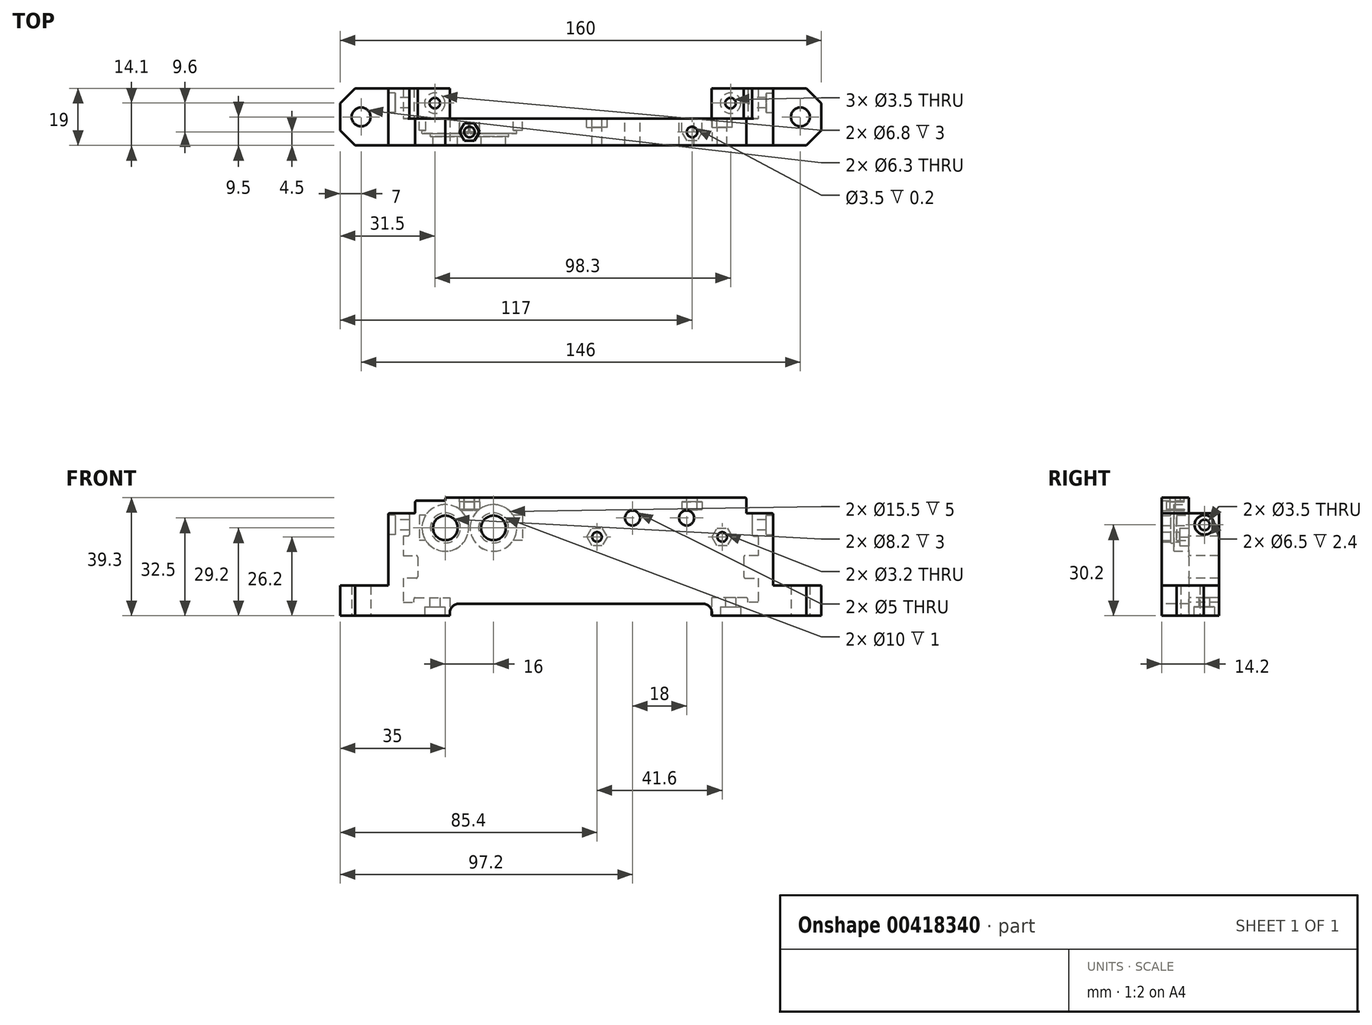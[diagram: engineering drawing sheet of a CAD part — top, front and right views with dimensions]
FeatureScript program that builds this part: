
annotation { "Feature Type Name" : "Feature", "Feature Type Description" : "" }
export const myFeature = defineFeature(function(context is Context, id is Id, definition is map)
    precondition{}
    {
        {
            var Q0;
            Q0=qCreatedBy(makeId("Front.planeOp"),FACE);
            var sketch = newSketch(context, id + "F0", { "sketchPlane" : qUnion([Q0])});
            skLineSegment(sketch, "E0", {"start": v(-64, 28) * mm, "end": v(-57.5, 28) * mm});
            skLineSegment(sketch, "E1", {"start": v(-57, 27.5) * mm, "end": v(-57, 21) * mm});
            skLineSegment(sketch, "E2", {"start": v(-57.5, 20.5) * mm, "end": v(-59, 20.5) * mm});
            skLineSegment(sketch, "E3", {"start": v(-59, 20.5) * mm, "end": v(-59, 14) * mm});
            skLineSegment(sketch, "E4", {"start": v(-59, 14) * mm, "end": v(-54.7, 14) * mm});
            skLineSegment(sketch, "E5", {"start": v(-54.2, 13.5) * mm, "end": v(-54.2, 7) * mm});
            skLineSegment(sketch, "E6", {"start": v(-54.7, 6.5) * mm, "end": v(-59, 6.5) * mm});
            skLineSegment(sketch, "E7", {"start": v(-59, 6.5) * mm, "end": v(-59, -1.5) * mm});
            skLineSegment(sketch, "E8", {"start": v(-59, -1.5) * mm, "end": v(-55.5, -1.5) * mm});
            skLineSegment(sketch, "E9", {"start": v(-55.5, -1.5) * mm, "end": v(-55.5, -0.5) * mm});
            skLineSegment(sketch, "E10", {"start": v(-55, 0) * mm, "end": v(-43.5, 0) * mm});
            skLineSegment(sketch, "E11", {"start": v(-43.5, 0) * mm, "end": v(-43.5, -6) * mm});
            skLineSegment(sketch, "E12", {"start": v(-43.5, -6) * mm, "end": v(-64, -6) * mm});
            skLineSegment(sketch, "E13", {"start": v(-64, -6) * mm, "end": v(-64, 28) * mm});
            skLineSegment(sketch, "E14", {"start": v(0, 0) * mm, "end": v(0, 39.92) * mm, "construction": true});
            skPoint(sketch, "E15.visualSharp", {"position": v(-54.2, 14) * mm});
            skArc(sketch, "E15.filletArc", {"start": v(-54.2, 13.5) * mm, "mid": v(-54.35, 13.85) * mm, "end": v(-54.7, 14) * mm});
            skPoint(sketch, "E16.visualSharp", {"position": v(-54.2, 6.5) * mm});
            skArc(sketch, "E16.filletArc", {"start": v(-54.7, 6.5) * mm, "mid": v(-54.35, 6.65) * mm, "end": v(-54.2, 7) * mm});
            skPoint(sketch, "E17.visualSharp", {"position": v(-55.5, 0) * mm});
            skArc(sketch, "E17.filletArc", {"start": v(-55, 0) * mm, "mid": v(-55.35, -0.15) * mm, "end": v(-55.5, -0.5) * mm});
            skPoint(sketch, "E18.visualSharp", {"position": v(-57, 28) * mm});
            skArc(sketch, "E18.filletArc", {"start": v(-57, 27.5) * mm, "mid": v(-57.15, 27.85) * mm, "end": v(-57.5, 28) * mm});
            skPoint(sketch, "E19.visualSharp", {"position": v(-57, 20.5) * mm});
            skArc(sketch, "E19.filletArc", {"start": v(-57.5, 20.5) * mm, "mid": v(-57.15, 20.65) * mm, "end": v(-57, 21) * mm});
            skLineSegment(sketch, "E20.MirrorCS", {"start": v(64, -6) * mm, "end": v(64, 28) * mm});
            skLineSegment(sketch, "E21.MirrorCS", {"start": v(43.5, -6) * mm, "end": v(64, -6) * mm});
            skLineSegment(sketch, "E22.MirrorCS", {"start": v(43.5, 0) * mm, "end": v(43.5, -6) * mm});
            skLineSegment(sketch, "E23.MirrorCS", {"start": v(55, 0) * mm, "end": v(43.5, 0) * mm});
            skArc(sketch, "E24.MirrorCS", {"start": v(55, 0) * mm, "mid": v(55.35, -0.15) * mm, "end": v(55.5, -0.5) * mm});
            skLineSegment(sketch, "E25.MirrorCS", {"start": v(55.5, -1.5) * mm, "end": v(55.5, -0.5) * mm});
            skLineSegment(sketch, "E26.MirrorCS", {"start": v(59, -1.5) * mm, "end": v(55.5, -1.5) * mm});
            skLineSegment(sketch, "E27.MirrorCS", {"start": v(59, 6.5) * mm, "end": v(59, -1.5) * mm});
            skLineSegment(sketch, "E28.MirrorCS", {"start": v(54.7, 6.5) * mm, "end": v(59, 6.5) * mm});
            skArc(sketch, "E29.MirrorCS", {"start": v(54.7, 6.5) * mm, "mid": v(54.35, 6.65) * mm, "end": v(54.2, 7) * mm});
            skLineSegment(sketch, "E30.MirrorCS", {"start": v(54.2, 13.5) * mm, "end": v(54.2, 7) * mm});
            skArc(sketch, "E31.MirrorCS", {"start": v(54.2, 13.5) * mm, "mid": v(54.35, 13.85) * mm, "end": v(54.7, 14) * mm});
            skLineSegment(sketch, "E32.MirrorCS", {"start": v(59, 14) * mm, "end": v(54.7, 14) * mm});
            skLineSegment(sketch, "E33.MirrorCS", {"start": v(59, 20.5) * mm, "end": v(59, 14) * mm});
            skLineSegment(sketch, "E34.MirrorCS", {"start": v(57.5, 20.5) * mm, "end": v(59, 20.5) * mm});
            skArc(sketch, "E35.MirrorCS", {"start": v(57.5, 20.5) * mm, "mid": v(57.15, 20.65) * mm, "end": v(57, 21) * mm});
            skLineSegment(sketch, "E36.MirrorCS", {"start": v(57, 27.5) * mm, "end": v(57, 21) * mm});
            skArc(sketch, "E37.MirrorCS", {"start": v(57, 27.5) * mm, "mid": v(57.15, 27.85) * mm, "end": v(57.5, 28) * mm});
            skLineSegment(sketch, "E38.MirrorCS", {"start": v(64, 28) * mm, "end": v(57.5, 28) * mm});
            skSolve(sketch);
        }
        {
            var Q0;
            Q0=makeQuery(id+"F0.imprint","IMPRINT",FACE,{"disambiguationData":[TD([[makeQuery(id+"F0.imprint","IMPRINT",EDGE,{"derivedFrom":sQuery(id+"F0.wireOp",EDGE,"E0")}),-1.0]])]});
            var sketch = newSketch(context, id + "F1", { "sketchPlane" : qUnion([Q0])});
            skLineSegment(sketch, "E39", {"start": v(-64, 28) * mm, "end": v(-64, -6) * mm});
            skLineSegment(sketch, "E40", {"start": v(-64, -6) * mm, "end": v(0, -6) * mm});
            skLineSegment(sketch, "E41", {"start": v(-64, 28) * mm, "end": v(-55, 28) * mm});
            skLineSegment(sketch, "E42", {"start": v(-55, 28) * mm, "end": v(-55, 32.2) * mm});
            skLineSegment(sketch, "E43", {"start": v(-55, 32.2) * mm, "end": v(0, 32.2) * mm});
            skLineSegment(sketch, "E44.MirrorCS", {"start": v(55, 32.2) * mm, "end": v(0, 32.2) * mm});
            skLineSegment(sketch, "E45.MirrorCS", {"start": v(64, -6) * mm, "end": v(0, -6) * mm});
            skLineSegment(sketch, "E46.MirrorCS", {"start": v(64, 28) * mm, "end": v(64, -6) * mm});
            skLineSegment(sketch, "E47.MirrorCS", {"start": v(64, 28) * mm, "end": v(55, 28) * mm});
            skLineSegment(sketch, "E48.MirrorCS", {"start": v(55, 28) * mm, "end": v(55, 32.2) * mm});
            skSolve(sketch);
        }
        {
            var Q0;
            Q0 = qSketchRegion(id + "F1", true);
            extrude(context, id + "F2", {"entities" : qUnion([Q0]), "depth" : 9 * mm});
        }
        {
            var Q0;
            Q0 = qSketchRegion(id + "F0", true);
            extrude(context, id + "F3", {"entities" : qUnion([Q0]), "operationType" : NewBodyOperationType.ADD, "oppositeDirection" : true, "depth" : 10 * mm});
        }
        {
            var Q0;
            Q0=qCreatedBy(makeId("Front.planeOp"),FACE);
            var sketch = newSketch(context, id + "F4", { "sketchPlane" : qUnion([Q0])});
            skCircle(sketch, "E49", {"center": v(-29, 23.2) * mm, "radius": 4.1 * mm});
            skCircle(sketch, "E50", {"center": v(-45, 23.2) * mm, "radius": 4.1 * mm});
            skCircle(sketch, "E51", {"center": v(47, 20.2) * mm, "radius": 1.6 * mm});
            skCircle(sketch, "E52", {"center": v(5.4, 20.2) * mm, "radius": 1.6 * mm});
            skCircle(sketch, "E53.cCircle", {"center": v(5.4, 20.2) * mm, "radius": 2.93 * mm, "construction": true});
            skLineSegment(sketch, "E53.0", {"start": v(7.09, 17.28) * mm, "end": v(3.71, 17.28) * mm});
            skLineSegment(sketch, "E53.1", {"start": v(3.71, 17.28) * mm, "end": v(2.02, 20.2) * mm});
            skLineSegment(sketch, "E53.2", {"start": v(2.02, 20.2) * mm, "end": v(3.71, 23.13) * mm});
            skLineSegment(sketch, "E53.3", {"start": v(3.71, 23.13) * mm, "end": v(7.09, 23.13) * mm});
            skLineSegment(sketch, "E53.4", {"start": v(7.09, 23.13) * mm, "end": v(8.78, 20.2) * mm});
            skLineSegment(sketch, "E53.5", {"start": v(8.78, 20.2) * mm, "end": v(7.09, 17.28) * mm});
            skPoint(sketch, "E53.0.midPoint", {"position": v(5.4, 17.28) * mm});
            skCircle(sketch, "E54.cCircle", {"center": v(47, 20.2) * mm, "radius": 2.93 * mm, "construction": true});
            skLineSegment(sketch, "E54.0", {"start": v(48.69, 17.28) * mm, "end": v(45.31, 17.28) * mm});
            skLineSegment(sketch, "E54.1", {"start": v(45.31, 17.28) * mm, "end": v(43.62, 20.2) * mm});
            skLineSegment(sketch, "E54.2", {"start": v(43.62, 20.2) * mm, "end": v(45.31, 23.13) * mm});
            skLineSegment(sketch, "E54.3", {"start": v(45.31, 23.13) * mm, "end": v(48.69, 23.13) * mm});
            skLineSegment(sketch, "E54.4", {"start": v(48.69, 23.13) * mm, "end": v(50.38, 20.2) * mm});
            skLineSegment(sketch, "E54.5", {"start": v(50.38, 20.2) * mm, "end": v(48.69, 17.28) * mm});
            skPoint(sketch, "E54.0.midPoint", {"position": v(47, 17.28) * mm});
            skCircle(sketch, "E55", {"center": v(-45, 23.2) * mm, "radius": 5 * mm});
            skCircle(sketch, "E56", {"center": v(-29, 23.2) * mm, "radius": 5 * mm});
            skCircle(sketch, "E57", {"center": v(35.2, 26.5) * mm, "radius": 2.5 * mm});
            skCircle(sketch, "E58", {"center": v(17.2, 26.5) * mm, "radius": 2.5 * mm});
            skCircle(sketch, "E59", {"center": v(-45, 23.2) * mm, "radius": 7.75 * mm});
            skCircle(sketch, "E60", {"center": v(-29, 23.2) * mm, "radius": 7.75 * mm});
            skSolve(sketch);
        }
        {
            var Q0;
            Q0=makeQuery(id+"F4.imprint","IMPRINT",FACE,{"disambiguationData":[TD([[makeQuery(id+"F4.imprint","IMPRINT",EDGE,{"derivedFrom":sQuery(id+"F4.wireOp",EDGE,"E49")}),1.0]])]});
            var Q1;
            Q1=makeQuery(id+"F4.imprint","IMPRINT",FACE,{"disambiguationData":[TD([[makeQuery(id+"F4.imprint","IMPRINT",EDGE,{"derivedFrom":sQuery(id+"F4.wireOp",EDGE,"E50")}),1.0]])]});
            var Q2;
            Q2=makeQuery(id+"F4.imprint","IMPRINT",FACE,{"disambiguationData":[TD([[makeQuery(id+"F4.imprint","IMPRINT",EDGE,{"derivedFrom":sQuery(id+"F4.wireOp",EDGE,"E57")}),1.0]])]});
            var Q3;
            Q3=makeQuery(id+"F4.imprint","IMPRINT",FACE,{"disambiguationData":[TD([[makeQuery(id+"F4.imprint","IMPRINT",EDGE,{"derivedFrom":sQuery(id+"F4.wireOp",EDGE,"E58")}),1.0]])]});
            var Q4;
            Q4=makeQuery(id+"F4.imprint","IMPRINT",FACE,{"disambiguationData":[TD([[makeQuery(id+"F4.imprint","IMPRINT",EDGE,{"derivedFrom":sQuery(id+"F4.wireOp",EDGE,"E52")}),1.0]])]});
            var Q5;
            Q5=makeQuery(id+"F4.imprint","IMPRINT",FACE,{"disambiguationData":[TD([[makeQuery(id+"F4.imprint","IMPRINT",EDGE,{"derivedFrom":sQuery(id+"F4.wireOp",EDGE,"E51")}),1.0]])]});
            extrude(context, id + "F5", {"entities" : qUnion([Q0, Q1, Q2, Q3, Q4, Q5]), "operationType" : NewBodyOperationType.REMOVE, "depth" : 24.8 * mm});
        }
        {
            var Q0;
            Q0=makeQuery(id+"F4.imprint","IMPRINT",FACE,{"disambiguationData":[TD([[makeQuery(id+"F4.imprint","IMPRINT",EDGE,{"derivedFrom":sQuery(id+"F4.wireOp",EDGE,"E52")}),-1.0]])]});
            var Q1;
            Q1=makeQuery(id+"F4.imprint","IMPRINT",FACE,{"disambiguationData":[TD([[makeQuery(id+"F4.imprint","IMPRINT",EDGE,{"derivedFrom":sQuery(id+"F4.wireOp",EDGE,"E51")}),-1.0]])]});
            extrude(context, id + "F6", {"entities" : qUnion([Q0, Q1]), "operationType" : NewBodyOperationType.REMOVE, "depth" : 3 * mm});
        }
        {
            var Q0;
            Q0=makeQuery(id+"F4.imprint","IMPRINT",FACE,{"disambiguationData":[TD([[makeQuery(id+"F4.imprint","IMPRINT",EDGE,{"derivedFrom":sQuery(id+"F4.wireOp",EDGE,"E50")}),-1.0]])]});
            var Q1;
            Q1=makeQuery(id+"F4.imprint","IMPRINT",FACE,{"disambiguationData":[TD([[makeQuery(id+"F4.imprint","IMPRINT",EDGE,{"derivedFrom":sQuery(id+"F4.wireOp",EDGE,"E49")}),-1.0]])]});
            extrude(context, id + "F7", {"entities" : qUnion([Q0, Q1]), "operationType" : NewBodyOperationType.REMOVE, "depth" : 6 * mm});
        }
        {
            var Q0;
            Q0=makeQuery(id+"F4.imprint","IMPRINT",FACE,{"disambiguationData":[TD([[makeQuery(id+"F4.imprint","IMPRINT",EDGE,{"derivedFrom":sQuery(id+"F4.wireOp",EDGE,"E56")}),-1.0]])]});
            var Q1;
            Q1=makeQuery(id+"F4.imprint","IMPRINT",FACE,{"disambiguationData":[TD([[makeQuery(id+"F4.imprint","IMPRINT",EDGE,{"derivedFrom":sQuery(id+"F4.wireOp",EDGE,"E55")}),-1.0]])]});
            extrude(context, id + "F8", {"entities" : qUnion([Q0, Q1]), "operationType" : NewBodyOperationType.REMOVE, "depth" : 5 * mm});
        }
        {
            var Q0;
            Q0=makeQuery(id+"F3.boolean.opBoolean","MERGE",FACE,{"derivedFrom":[makeQuery(id+"F2.opExtrude","SWEPT_FACE",FACE,{"disambiguationData":[OSD([sQuery(id+"F1.wireOp",EDGE,"E39")])]}),makeQuery(id+"F3.opExtrude","SWEPT_FACE",FACE,{"disambiguationData":[OSD([sQuery(id+"F0.wireOp",EDGE,"E13")])]})]});
            var sketch = newSketch(context, id + "F9", { "sketchPlane" : qUnion([Q0])});
            skCircle(sketch, "E61", {"center": v(-5.2, 24.2) * mm, "radius": 1.75 * mm});
            skCircle(sketch, "E62", {"center": v(-5.2, 24.2) * mm, "radius": 3.25 * mm});
            skSolve(sketch);
        }
        {
            var Q0;
            Q0=makeQuery(id+"F9.imprint","IMPRINT",FACE,{"disambiguationData":[TD([[makeQuery(id+"F9.imprint","IMPRINT",EDGE,{"derivedFrom":sQuery(id+"F9.wireOp",EDGE,"E61")}),1.0]])]});
            extrude(context, id + "F10", {"entities" : qUnion([Q0]), "operationType" : NewBodyOperationType.REMOVE, "oppositeDirection" : true, "depth" : 158.2 * mm});
        }
        {
            var Q0;
            Q0=makeQuery(id+"F9.imprint","IMPRINT",FACE,{"disambiguationData":[TD([[makeQuery(id+"F9.imprint","IMPRINT",EDGE,{"derivedFrom":sQuery(id+"F9.wireOp",EDGE,"E61")}),-1.0]])]});
            extrude(context, id + "F11", {"entities" : qUnion([Q0]), "operationType" : NewBodyOperationType.REMOVE, "oppositeDirection" : true, "depth" : 2.4 * mm});
        }
        {
            var Q0;
            Q0=makeQuery(id+"F3.boolean.opBoolean","MERGE",FACE,{"derivedFrom":[makeQuery(id+"F2.opExtrude","SWEPT_FACE",FACE,{"disambiguationData":[OSD([sQuery(id+"F1.wireOp",EDGE,"E46.MirrorCS")])]}),makeQuery(id+"F3.opExtrude","SWEPT_FACE",FACE,{"disambiguationData":[OSD([sQuery(id+"F0.wireOp",EDGE,"E20.MirrorCS")])]})]});
            var sketch = newSketch(context, id + "F12", { "sketchPlane" : qUnion([Q0])});
            skCircle(sketch, "E63", {"center": v(5.2, 24.2) * mm, "radius": 3.25 * mm});
            skSolve(sketch);
        }
        {
            var Q0;
            Q0 = qSketchRegion(id + "F12", true);
            extrude(context, id + "F13", {"entities" : qUnion([Q0]), "operationType" : NewBodyOperationType.REMOVE, "oppositeDirection" : true, "depth" : 2.4 * mm});
        }
        {
            var Q0;
            Q0=makeQuery(id+"F3.boolean.opBoolean","MERGE",FACE,{"derivedFrom":[makeQuery(id+"F2.opExtrude","SWEPT_FACE",FACE,{"disambiguationData":[OSD([sQuery(id+"F1.wireOp",EDGE,"E40"),sQuery(id+"F1.wireOp",EDGE,"E45.MirrorCS")])]}),makeQuery(id+"F3.opExtrude","SWEPT_FACE",FACE,{"disambiguationData":[OSD([sQuery(id+"F0.wireOp",EDGE,"E12")])]}),makeQuery(id+"F3.opExtrude","SWEPT_FACE",FACE,{"disambiguationData":[OSD([sQuery(id+"F0.wireOp",EDGE,"E21.MirrorCS")])]})]});
            var sketch = newSketch(context, id + "F14", { "sketchPlane" : qUnion([Q0])});
            skCircle(sketch, "E64", {"center": v(49.8, -5.1) * mm, "radius": 1.75 * mm});
            skCircle(sketch, "E65", {"center": v(49.8, -5.1) * mm, "radius": 3.4 * mm});
            skCircle(sketch, "E66", {"center": v(-48.5, -5.1) * mm, "radius": 1.75 * mm});
            skCircle(sketch, "E67", {"center": v(-48.5, -5.1) * mm, "radius": 3.4 * mm});
            skSolve(sketch);
        }
        {
            var Q0;
            Q0 = qSketchRegion(id + "F14", true);
            var Q1;
            Q1=makeQuery(id+"F14.imprint","IMPRINT",FACE,{"disambiguationData":[TD([[makeQuery(id+"F14.imprint","IMPRINT",EDGE,{"derivedFrom":sQuery(id+"F14.wireOp",EDGE,"E64")}),1.0]])]});
            extrude(context, id + "F15", {"entities" : qUnion([Q0, Q1]), "operationType" : NewBodyOperationType.REMOVE, "oppositeDirection" : true, "depth" : 3 * mm});
        }
        {
            var Q0;
            Q0=makeQuery(id+"F14.imprint","IMPRINT",FACE,{"disambiguationData":[TD([[makeQuery(id+"F14.imprint","IMPRINT",EDGE,{"derivedFrom":sQuery(id+"F14.wireOp",EDGE,"E64")}),1.0]])]});
            var Q1;
            Q1=makeQuery(id+"F14.imprint","IMPRINT",FACE,{"disambiguationData":[TD([[makeQuery(id+"F14.imprint","IMPRINT",EDGE,{"derivedFrom":sQuery(id+"F14.wireOp",EDGE,"E66")}),1.0]])]});
            extrude(context, id + "F16", {"entities" : qUnion([Q0, Q1]), "operationType" : NewBodyOperationType.REMOVE, "oppositeDirection" : true, "depth" : 25 * mm});
        }
        {
            var Q0;
            Q0=makeQuery(id+"F2.opExtrude","SWEPT_FACE",FACE,{"disambiguationData":[OSD([sQuery(id+"F1.wireOp",EDGE,"E43"),sQuery(id+"F1.wireOp",EDGE,"E44.MirrorCS")])]});
            var sketch = newSketch(context, id + "F17", { "sketchPlane" : qUnion([Q0])});
            skLineSegment(sketch, "E68.bottom", {"start": v(55, -9) * mm, "end": v(-45, -9) * mm});
            skLineSegment(sketch, "E68.top", {"start": v(55, 0) * mm, "end": v(-45, 0) * mm});
            skLineSegment(sketch, "E68.left", {"start": v(55, -9) * mm, "end": v(55, 0) * mm});
            skLineSegment(sketch, "E68.right", {"start": v(-45, -9) * mm, "end": v(-45, 0) * mm});
            skSolve(sketch);
        }
        {
            var Q0;
            Q0 = qSketchRegion(id + "F17", true);
            extrude(context, id + "F18", {"entities" : qUnion([Q0]), "operationType" : NewBodyOperationType.ADD, "depth" : 1.1 * mm});
        }
        {
            var Q0;
            Q0=makeQuery(id+"F18.opExtrude","CAP_FACE",FACE,{"disambiguationData":[OSD([sQuery(id+"F17.wireOp",EDGE,"E68.bottom"),sQuery(id+"F17.wireOp",EDGE,"E68.top"),sQuery(id+"F17.wireOp",EDGE,"E68.left"),sQuery(id+"F17.wireOp",EDGE,"E68.right")])],"isStart":false});
            var sketch = newSketch(context, id + "F19", { "sketchPlane" : qUnion([Q0])});
            skCircle(sketch, "E69", {"center": v(37, -4.5) * mm, "radius": 1.75 * mm});
            skCircle(sketch, "E70.cCircle", {"center": v(37, -4.5) * mm, "radius": 2.93 * mm, "construction": true});
            skLineSegment(sketch, "E70.0", {"start": v(38.69, -7.42) * mm, "end": v(35.31, -7.42) * mm});
            skLineSegment(sketch, "E70.1", {"start": v(35.31, -7.42) * mm, "end": v(33.62, -4.5) * mm});
            skLineSegment(sketch, "E70.2", {"start": v(33.62, -4.5) * mm, "end": v(35.31, -1.57) * mm});
            skLineSegment(sketch, "E70.3", {"start": v(35.31, -1.57) * mm, "end": v(38.69, -1.57) * mm});
            skLineSegment(sketch, "E70.4", {"start": v(38.69, -1.58) * mm, "end": v(40.38, -4.5) * mm});
            skLineSegment(sketch, "E70.5", {"start": v(40.38, -4.5) * mm, "end": v(38.69, -7.42) * mm});
            skPoint(sketch, "E70.0.midPoint", {"position": v(37, -7.42) * mm});
            skLineSegment(sketch, "E71", {"start": v(0, 6.74) * mm, "end": v(0, -15.63) * mm, "construction": true});
            skCircle(sketch, "E72.MirrorC", {"center": v(-37, -4.5) * mm, "radius": 1.75 * mm});
            skLineSegment(sketch, "E73.MirrorCS", {"start": v(-35.31, -7.43) * mm, "end": v(-33.62, -4.5) * mm});
            skLineSegment(sketch, "E74.MirrorCS", {"start": v(-33.62, -4.5) * mm, "end": v(-35.31, -1.58) * mm});
            skLineSegment(sketch, "E75.MirrorCS", {"start": v(-35.31, -1.58) * mm, "end": v(-38.69, -1.58) * mm});
            skLineSegment(sketch, "E76.MirrorCS", {"start": v(-38.69, -1.58) * mm, "end": v(-40.38, -4.5) * mm});
            skLineSegment(sketch, "E77.MirrorCS", {"start": v(-40.38, -4.5) * mm, "end": v(-38.69, -7.43) * mm});
            skLineSegment(sketch, "E78.MirrorCS", {"start": v(-38.69, -7.43) * mm, "end": v(-35.31, -7.43) * mm});
            skSolve(sketch);
        }
        {
            var Q0;
            Q0 = qSketchRegion(id + "F19", true);
            extrude(context, id + "F20", {"entities" : qUnion([Q0]), "operationType" : NewBodyOperationType.REMOVE, "oppositeDirection" : true, "depth" : 4 * mm, "hasSecondDirection" : true, "secondDirectionOppositeDirection" : true, "secondDirectionDepth" : (3.9 - 2.5) * mm});
        }
        {
            var Q0;
            Q0=makeQuery(id+"F19.imprint","IMPRINT",FACE,{"disambiguationData":[TD([[makeQuery(id+"F19.imprint","IMPRINT",EDGE,{"derivedFrom":sQuery(id+"F19.wireOp",EDGE,"E72.MirrorC")}),-1.0]])]});
            var Q1;
            Q1=makeQuery(id+"F19.imprint","IMPRINT",FACE,{"disambiguationData":[TD([[makeQuery(id+"F19.imprint","IMPRINT",EDGE,{"derivedFrom":sQuery(id+"F19.wireOp",EDGE,"E69")}),1.0]])]});
            extrude(context, id + "F21", {"entities" : qUnion([Q0, Q1]), "operationType" : NewBodyOperationType.REMOVE, "oppositeDirection" : true, "depth" : 4.2 * mm});
        }
        {
            var Q0;
            Q0=makeQuery(id+"F18.boolean.opBoolean","MERGE",FACE,{"derivedFrom":[makeQuery(id+"F2.opExtrude","CAP_FACE",FACE,{"disambiguationData":[OSD([sQuery(id+"F1.wireOp",EDGE,"E39"),sQuery(id+"F1.wireOp",EDGE,"E40"),sQuery(id+"F1.wireOp",EDGE,"E41"),sQuery(id+"F1.wireOp",EDGE,"E42"),sQuery(id+"F1.wireOp",EDGE,"E43"),sQuery(id+"F1.wireOp",EDGE,"E44.MirrorCS"),sQuery(id+"F1.wireOp",EDGE,"E45.MirrorCS"),sQuery(id+"F1.wireOp",EDGE,"E46.MirrorCS"),sQuery(id+"F1.wireOp",EDGE,"E47.MirrorCS"),sQuery(id+"F1.wireOp",EDGE,"E48.MirrorCS")])],"isStart":true}),makeQuery(id+"F18.opExtrude","SWEPT_FACE",FACE,{"disambiguationData":[OSD([sQuery(id+"F17.wireOp",EDGE,"E68.top")])]})]});
            var sketch = newSketch(context, id + "F22", { "sketchPlane" : qUnion([Q0])});
            skLineSegment(sketch, "E79.bottom", {"start": v(-33.62, 31.9) * mm, "end": v(-40.38, 31.9) * mm});
            skLineSegment(sketch, "E79.top", {"start": v(-33.62, 29.3) * mm, "end": v(-40.38, 29.3) * mm});
            skLineSegment(sketch, "E79.left", {"start": v(-33.62, 31.9) * mm, "end": v(-33.62, 29.3) * mm});
            skLineSegment(sketch, "E79.right", {"start": v(-40.38, 31.9) * mm, "end": v(-40.38, 29.3) * mm});
            skLineSegment(sketch, "E80.bottom", {"start": v(33.62, 31.9) * mm, "end": v(40.38, 31.9) * mm});
            skLineSegment(sketch, "E80.top", {"start": v(33.62, 29.3) * mm, "end": v(40.38, 29.3) * mm});
            skLineSegment(sketch, "E80.left", {"start": v(33.62, 31.9) * mm, "end": v(33.62, 29.3) * mm});
            skLineSegment(sketch, "E80.right", {"start": v(40.38, 31.9) * mm, "end": v(40.38, 29.3) * mm});
            skSolve(sketch);
        }
        {
            var Q0;
            Q0 = qSketchRegion(id + "F22", true);
            extrude(context, id + "F23", {"entities" : qUnion([Q0]), "operationType" : NewBodyOperationType.REMOVE, "oppositeDirection" : true, "depth" : 4.5 * mm});
        }
        {
            var Q0;
            Q0=makeQuery(id+"F9.imprint","IMPRINT",FACE,{"disambiguationData":[TD([[makeQuery(id+"F9.imprint","IMPRINT",EDGE,{"derivedFrom":sQuery(id+"F9.wireOp",EDGE,"E62")}),-1.0]])]});
            var sketch = newSketch(context, id + "F24", { "sketchPlane" : qUnion([Q0])});
            skLineSegment(sketch, "E81.bottom", {"start": v(9, -6) * mm, "end": v(-10, -6) * mm});
            skLineSegment(sketch, "E81.top", {"start": v(9, 4) * mm, "end": v(-10, 4) * mm});
            skLineSegment(sketch, "E81.left", {"start": v(9, -6) * mm, "end": v(9, 4) * mm});
            skLineSegment(sketch, "E81.right", {"start": v(-10, -6) * mm, "end": v(-10, 4) * mm});
            skSolve(sketch);
        }
        {
            var Q0;
            Q0 = qSketchRegion(id + "F24", true);
            extrude(context, id + "F25", {"entities" : qUnion([Q0]), "operationType" : NewBodyOperationType.ADD, "depth" : 16 * mm});
        }
        {
            var Q0;
            Q0=makeQuery(id+"F25.opExtrude","CAP_EDGE",EDGE,{"disambiguationData":[OSD([sQuery(id+"F24.wireOp",EDGE,"E81.left")])],"isStart":false});
            var Q1;
            Q1=makeQuery(id+"F25.opExtrude","CAP_EDGE",EDGE,{"disambiguationData":[OSD([sQuery(id+"F24.wireOp",EDGE,"E81.right")])],"isStart":false});
            chamfer(context, id + "F26", {"entities" : qUnion([Q0, Q1]), "width" : 5 * mm, "tangentPropagation" : true});
        }
        {
            var Q0;
            Q0=makeQuery(id+"F3.boolean.opBoolean","MERGE",FACE,{"derivedFrom":[makeQuery(id+"F2.opExtrude","SWEPT_FACE",FACE,{"disambiguationData":[OSD([sQuery(id+"F1.wireOp",EDGE,"E46.MirrorCS")])]}),makeQuery(id+"F3.opExtrude","SWEPT_FACE",FACE,{"disambiguationData":[OSD([sQuery(id+"F0.wireOp",EDGE,"E20.MirrorCS")])]})]});
            var sketch = newSketch(context, id + "F27", { "sketchPlane" : qUnion([Q0])});
            skLineSegment(sketch, "E82.bottom", {"start": v(-9, -6) * mm, "end": v(10, -6) * mm});
            skLineSegment(sketch, "E82.top", {"start": v(-9, 4) * mm, "end": v(10, 4) * mm});
            skLineSegment(sketch, "E82.left", {"start": v(-9, -6) * mm, "end": v(-9, 4) * mm});
            skLineSegment(sketch, "E82.right", {"start": v(10, -6) * mm, "end": v(10, 4) * mm});
            skSolve(sketch);
        }
        {
            var Q0;
            Q0 = qSketchRegion(id + "F27", true);
            extrude(context, id + "F28", {"entities" : qUnion([Q0]), "operationType" : NewBodyOperationType.ADD, "depth" : 16 * mm});
        }
        {
            var Q0;
            Q0=makeQuery(id+"F28.opExtrude","CAP_EDGE",EDGE,{"disambiguationData":[OSD([sQuery(id+"F27.wireOp",EDGE,"E82.right")])],"isStart":false});
            var Q1;
            Q1=makeQuery(id+"F28.opExtrude","CAP_EDGE",EDGE,{"disambiguationData":[OSD([sQuery(id+"F27.wireOp",EDGE,"E82.left")])],"isStart":false});
            chamfer(context, id + "F29", {"entities" : qUnion([Q0, Q1]), "width" : 5 * mm, "tangentPropagation" : true});
        }
        {
            var Q0;
            {var subQ1=sQuery(id+"F0.wireOp",EDGE,"E21.MirrorCS");var subQ7=sQuery(id+"F1.wireOp",EDGE,"E45.MirrorCS");var subQ12=sQuery(id+"F1.wireOp",EDGE,"E40");var subQ13=sQuery(id+"F1.wireOp",EDGE,"E39");var subQ15=sQuery(id+"F0.wireOp",EDGE,"E12");Q0=makeQuery(id+"F28.boolean.opBoolean","MERGE",FACE,{"derivedFrom":[makeQuery(id+"F25.boolean.opBoolean","MERGE",FACE,{"derivedFrom":[makeQuery(id+"F15.boolean.opBoolean","SPLIT",FACE,{"disambiguationData":[TD([makeQuery(id+"F2.opExtrude","SWEPT_FACE",FACE,{"disambiguationData":[OSD([subQ13])]})])],"derivedFrom":makeQuery(id+"F3.boolean.opBoolean","MERGE",FACE,{"derivedFrom":[makeQuery(id+"F2.opExtrude","SWEPT_FACE",FACE,{"disambiguationData":[OSD([subQ12,subQ7])]}),makeQuery(id+"F3.opExtrude","SWEPT_FACE",FACE,{"disambiguationData":[OSD([subQ15])]}),makeQuery(id+"F3.opExtrude","SWEPT_FACE",FACE,{"disambiguationData":[OSD([subQ1])]})]})}),makeQuery(id+"F25.opExtrude","SWEPT_FACE",FACE,{"disambiguationData":[OSD([sQuery(id+"F24.wireOp",EDGE,"E81.bottom")])]})]}),makeQuery(id+"F28.opExtrude","SWEPT_FACE",FACE,{"disambiguationData":[OSD([sQuery(id+"F27.wireOp",EDGE,"E82.bottom")])]})]});}
            var sketch = newSketch(context, id + "F30", { "sketchPlane" : qUnion([Q0])});
            skCircle(sketch, "E83", {"center": v(-73, -0.5) * mm, "radius": 3.15 * mm});
            skPoint(sketch, "E83.centerSnap0", {"position": v(-80, -0.5) * mm});
            skCircle(sketch, "E84", {"center": v(73, -0.5) * mm, "radius": 3.15 * mm});
            skPoint(sketch, "E84.centerSnap0", {"position": v(80, -0.5) * mm});
            skSolve(sketch);
        }
        {
            var Q0;
            Q0 = qSketchRegion(id + "F30", true);
            extrude(context, id + "F31", {"entities" : qUnion([Q0]), "operationType" : NewBodyOperationType.REMOVE, "oppositeDirection" : true, "depth" : 25 * mm});
        }
        {
            var Q0;
            Q0=makeQuery(id+"F3.boolean.opBoolean","MERGE",EDGE,{"derivedFrom":[makeQuery(id+"F2.opExtrude","SWEPT_EDGE",EDGE,{"disambiguationData":[OSD([sQuery(id+"F1.wireOp",EDGE,"E46.MirrorCS"),sQuery(id+"F1.wireOp",EDGE,"E47.MirrorCS")])]}),makeQuery(id+"F3.opExtrude","SWEPT_EDGE",EDGE,{"disambiguationData":[OSD([sQuery(id+"F0.wireOp",EDGE,"E20.MirrorCS"),sQuery(id+"F0.wireOp",EDGE,"E38.MirrorCS")])]})]});
            var Q1;
            Q1=makeQuery(id+"F18.opExtrude","CAP_EDGE",EDGE,{"disambiguationData":[OSD([sQuery(id+"F17.wireOp",EDGE,"E68.left")])],"isStart":false});
            var Q2;
            Q2=makeQuery(id+"F3.boolean.opBoolean","MERGE",EDGE,{"derivedFrom":[makeQuery(id+"F2.opExtrude","SWEPT_EDGE",EDGE,{"disambiguationData":[OSD([sQuery(id+"F1.wireOp",EDGE,"E39"),sQuery(id+"F1.wireOp",EDGE,"E41")])]}),makeQuery(id+"F3.opExtrude","SWEPT_EDGE",EDGE,{"disambiguationData":[OSD([sQuery(id+"F0.wireOp",EDGE,"E0"),sQuery(id+"F0.wireOp",EDGE,"E13")])]})]});
            var Q3;
            Q3=makeQuery(id+"F2.opExtrude","SWEPT_EDGE",EDGE,{"disambiguationData":[OSD([sQuery(id+"F1.wireOp",EDGE,"E41"),sQuery(id+"F1.wireOp",EDGE,"E42")])]});
            var Q4;
            Q4=makeQuery(id+"F2.opExtrude","SWEPT_EDGE",EDGE,{"disambiguationData":[OSD([sQuery(id+"F1.wireOp",EDGE,"E42"),sQuery(id+"F1.wireOp",EDGE,"E43")])]});
            var Q5;
            Q5=makeQuery(id+"F18.opExtrude","CAP_EDGE",EDGE,{"disambiguationData":[OSD([sQuery(id+"F17.wireOp",EDGE,"E68.right")])],"isStart":true});
            var Q6;
            Q6=makeQuery(id+"F18.opExtrude","CAP_EDGE",EDGE,{"disambiguationData":[OSD([sQuery(id+"F17.wireOp",EDGE,"E68.right")])],"isStart":false});
            var Q7;
            Q7=makeQuery(id+"F25.opExtrude","CAP_EDGE",EDGE,{"disambiguationData":[OSD([sQuery(id+"F24.wireOp",EDGE,"E81.top")])],"isStart":true});
            var Q8;
            Q8=makeQuery(id+"F28.opExtrude","CAP_EDGE",EDGE,{"disambiguationData":[OSD([sQuery(id+"F27.wireOp",EDGE,"E82.top")])],"isStart":true});
            fillet(context, id + "F32", {"entities" : qUnion([Q0, Q1, Q2, Q3, Q4, Q5, Q6, Q7, Q8]), "radius" : 0.4 * mm, "tangentPropagation" : true, "allowEdgeOverflow" : false});
        }
        {
            var Q0;
            Q0=makeQuery(id+"F14.imprint","IMPRINT",FACE,{"disambiguationData":[TD([[makeQuery(id+"F14.imprint","IMPRINT",EDGE,{"derivedFrom":sQuery(id+"F14.wireOp",EDGE,"E65")}),-1.0]])]});
            var sketch = newSketch(context, id + "F33", { "sketchPlane" : qUnion([Q0])});
            skLineSegment(sketch, "E85.bottom", {"start": v(-43.5, 0) * mm, "end": v(43.62, 0) * mm});
            skLineSegment(sketch, "E85.top", {"start": v(-43.5, 9) * mm, "end": v(43.62, 9) * mm});
            skLineSegment(sketch, "E85.left", {"start": v(-43.5, 0) * mm, "end": v(-43.5, 9) * mm});
            skLineSegment(sketch, "E85.right", {"start": v(43.62, 0) * mm, "end": v(43.62, 9) * mm});
            skSolve(sketch);
        }
        {
            var Q0;
            Q0 = qSketchRegion(id + "F33", true);
            extrude(context, id + "F34", {"entities" : qUnion([Q0]), "operationType" : NewBodyOperationType.REMOVE, "oppositeDirection" : true, "depth" : 4 * mm});
        }
        {
            var Q0;
            Q0=makeQuery(id+"F34.boolean.opBoolean","COPY",EDGE,{"derivedFrom":makeQuery(id+"F34.opExtrude","CAP_EDGE",EDGE,{"disambiguationData":[OSD([sQuery(id+"F33.wireOp",EDGE,"E85.left")])],"isStart":false})});
            var Q1;
            Q1=makeQuery(id+"F34.boolean.opBoolean","COPY",EDGE,{"derivedFrom":makeQuery(id+"F34.opExtrude","CAP_EDGE",EDGE,{"disambiguationData":[OSD([sQuery(id+"F33.wireOp",EDGE,"E85.right")])],"isStart":false})});
            fillet(context, id + "F35", {"entities" : qUnion([Q0, Q1]), "radius" : 3 * mm, "tangentPropagation" : true, "allowEdgeOverflow" : false});
        }
        {
            var Q0;
            Q0=makeQuery(id+"F18.boolean.opBoolean","MERGE",FACE,{"derivedFrom":[makeQuery(id+"F2.opExtrude","CAP_FACE",FACE,{"disambiguationData":[OSD([sQuery(id+"F1.wireOp",EDGE,"E39"),sQuery(id+"F1.wireOp",EDGE,"E40"),sQuery(id+"F1.wireOp",EDGE,"E41"),sQuery(id+"F1.wireOp",EDGE,"E42"),sQuery(id+"F1.wireOp",EDGE,"E43"),sQuery(id+"F1.wireOp",EDGE,"E44.MirrorCS"),sQuery(id+"F1.wireOp",EDGE,"E45.MirrorCS"),sQuery(id+"F1.wireOp",EDGE,"E46.MirrorCS"),sQuery(id+"F1.wireOp",EDGE,"E47.MirrorCS"),sQuery(id+"F1.wireOp",EDGE,"E48.MirrorCS")])],"isStart":true}),makeQuery(id+"F18.opExtrude","SWEPT_FACE",FACE,{"disambiguationData":[OSD([sQuery(id+"F17.wireOp",EDGE,"E68.top")])]})]});
            var sketch = newSketch(context, id + "F36", { "sketchPlane" : qUnion([Q0])});
            skLineSegment(sketch, "E86.bottom", {"start": v(19.42, 27.36) * mm, "end": v(53.66, 27.36) * mm});
            skLineSegment(sketch, "E86.top", {"start": v(19.42, 19.06) * mm, "end": v(53.66, 19.06) * mm});
            skLineSegment(sketch, "E86.left", {"start": v(19.42, 27.36) * mm, "end": v(19.42, 19.06) * mm});
            skLineSegment(sketch, "E86.right", {"start": v(53.66, 27.36) * mm, "end": v(53.66, 19.06) * mm});
            skSolve(sketch);
        }
        {
            var Q0;
            {var subQ0=sQuery(id+"F36.wireOp",EDGE,"E86.bottom");var subQ1=makeQuery(id+"F8.boolean.opBoolean","COPY",EDGE,{"derivedFrom":makeQuery(id+"F8.opExtrude","CAP_EDGE",EDGE,{"disambiguationData":[OSD([sQuery(id+"F4.wireOp",EDGE,"E60")])],"isStart":true})});var subQ2=makeQuery(id+"F36.imprint","INTERSECT",VERTEX,{"disambiguationData":[OD(1.0)],"derivedFrom":[subQ1,subQ0]});Q0=makeQuery(id+"F36.imprint","IMPRINT",FACE,{"disambiguationData":[TD([[makeQuery(id+"F36.imprint","IMPRINT",EDGE,{"disambiguationData":[TD([[subQ2,-1.0]])],"derivedFrom":subQ0}),-1.0]])]});}
            var Q1;
            {var subQ0=sQuery(id+"F36.wireOp",EDGE,"E86.right");Q1=makeQuery(id+"F36.imprint","IMPRINT",FACE,{"disambiguationData":[TD([[makeQuery(id+"F36.imprint","IMPRINT",EDGE,{"derivedFrom":subQ0}),-1.0]])]});}
            var Q2;
            {var subQ0=sQuery(id+"F36.wireOp",EDGE,"E86.left");Q2=makeQuery(id+"F36.imprint","IMPRINT",FACE,{"disambiguationData":[TD([[makeQuery(id+"F36.imprint","IMPRINT",EDGE,{"derivedFrom":subQ0}),1.0]])]});}
            extrude(context, id + "F37", {"entities" : qUnion([Q0, Q1, Q2]), "operationType" : NewBodyOperationType.REMOVE, "oppositeDirection" : true, "depth" : 4 * mm});
        }
    });
